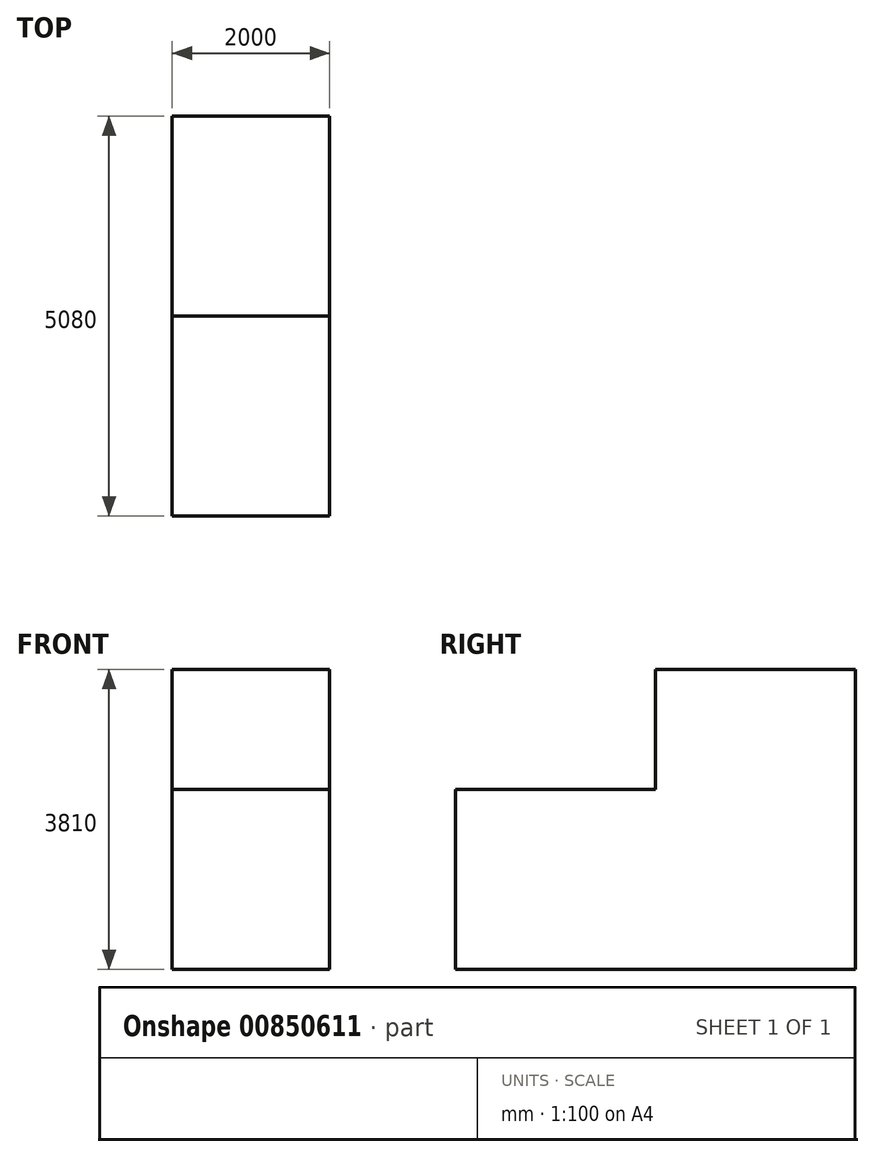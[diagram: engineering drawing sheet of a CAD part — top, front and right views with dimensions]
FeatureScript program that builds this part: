
annotation { "Feature Type Name" : "Feature", "Feature Type Description" : "" }
export const myFeature = defineFeature(function(context is Context, id is Id, definition is map)
    precondition{}
    {
        {
            var Q0;
            Q0=qCreatedBy(makeId("Right.planeOp"),FACE);
            var sketch = newSketch(context, id + "F0", { "sketchPlane" : qUnion([Q0])});
            skLineSegment(sketch, "E0", {"start": v(-118.73, 2232.26) * mm, "end": v(-118.73, -53.74) * mm});
            skLineSegment(sketch, "E1", {"start": v(-118.73, -53.74) * mm, "end": v(4961.27, -53.74) * mm});
            skLineSegment(sketch, "E2", {"start": v(4961.27, -53.74) * mm, "end": v(4961.27, 3756.26) * mm});
            skLineSegment(sketch, "E3", {"start": v(4961.27, 3756.26) * mm, "end": v(2421.27, 3756.26) * mm});
            skLineSegment(sketch, "E4", {"start": v(2421.27, 3756.26) * mm, "end": v(2421.27, 2232.26) * mm});
            skLineSegment(sketch, "E5", {"start": v(2421.27, 2232.26) * mm, "end": v(-118.73, 2232.26) * mm});
            skSolve(sketch);
        }
        {
            var Q0;
            Q0 = qSketchRegion(id + "F0", true);
            extrude(context, id + "F1", {"entities" : qUnion([Q0]), "depth" : 2000 * mm, "offsetDistance" : 25.4 * mm});
        }
    });
